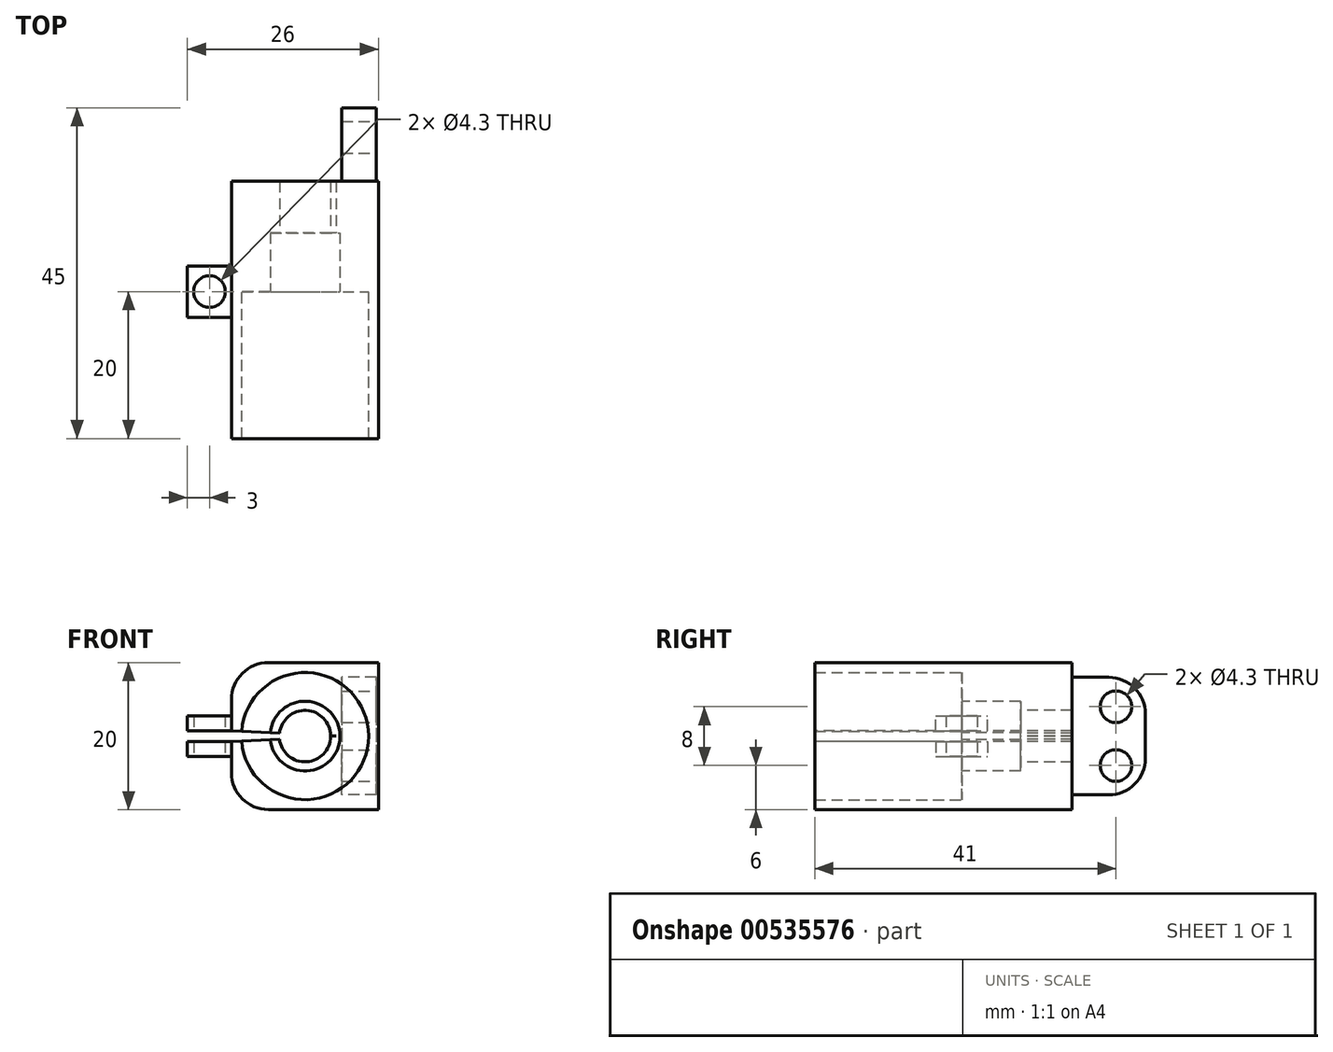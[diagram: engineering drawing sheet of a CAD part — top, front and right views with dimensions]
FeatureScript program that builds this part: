
annotation { "Feature Type Name" : "Feature", "Feature Type Description" : "" }
export const myFeature = defineFeature(function(context is Context, id is Id, definition is map)
    precondition{}
    {
        {
            var Q0;
            Q0=qCreatedBy(makeId("Front.planeOp"),FACE);
            var sketch = newSketch(context, id + "F0", { "sketchPlane" : qUnion([Q0])});
            skCircle(sketch, "E0", {"center": v(0, 0) * mm, "radius": 8.65 * mm});
            skLineSegment(sketch, "E1.bottom", {"start": v(-10, 10) * mm, "end": v(10, 10) * mm});
            skLineSegment(sketch, "E1.top", {"start": v(-10, -10) * mm, "end": v(10, -10) * mm});
            skLineSegment(sketch, "E1.left", {"start": v(-10, 10) * mm, "end": v(-10, -10) * mm});
            skLineSegment(sketch, "E1.right", {"start": v(10, 10) * mm, "end": v(10, -10) * mm});
            skSolve(sketch);
        }
        {
            var Q0;
            Q0=qSketchRegion(id+"F0",true);
            extrude(context, id + "F1", {"entities" : qUnion([Q0]), "depth" : 20 * mm, "offsetDistance" : 25 * mm});
        }
        {
            var Q0;
            Q0=qCreatedBy(makeId("Front.planeOp"),FACE);
            var sketch = newSketch(context, id + "F2", { "sketchPlane" : qUnion([Q0])});
            skLineSegment(sketch, "E2.bottom", {"start": v(10, 10) * mm, "end": v(-10, 10) * mm});
            skLineSegment(sketch, "E2.top", {"start": v(10, -10) * mm, "end": v(-10, -10) * mm});
            skLineSegment(sketch, "E2.left", {"start": v(10, 10) * mm, "end": v(10, -10) * mm});
            skLineSegment(sketch, "E2.right", {"start": v(-10, 10) * mm, "end": v(-10, -10) * mm});
            skPoint(sketch, "E2.middle", {"position": v(0, 0) * mm});
            skSolve(sketch);
        }
        {
            var Q0;
            Q0=qSketchRegion(id+"F2",true);
            extrude(context, id + "F3", {"entities" : qUnion([Q0]), "operationType" : NewBodyOperationType.ADD, "oppositeDirection" : true, "depth" : 15 * mm, "offsetDistance" : 25 * mm});
        }
        {
            var Q0;
            Q0=qCreatedBy(makeId("Front.planeOp"),FACE);
            var sketch = newSketch(context, id + "F4", { "sketchPlane" : qUnion([Q0])});
            skCircle(sketch, "E3", {"center": v(0, 0) * mm, "radius": 4.75 * mm});
            skSolve(sketch);
        }
        {
            var Q0;
            Q0=qSketchRegion(id+"F4",true);
            extrude(context, id + "F5", {"entities" : qUnion([Q0]), "operationType" : NewBodyOperationType.REMOVE, "oppositeDirection" : true, "depth" : 8 * mm, "offsetDistance" : 25 * mm});
        }
        {
            var Q0;
            Q0=qCreatedBy(makeId("Front.planeOp"),FACE);
            var sketch = newSketch(context, id + "F6", { "sketchPlane" : qUnion([Q0])});
            skCircle(sketch, "E4", {"center": v(0, 0) * mm, "radius": 2.08 * mm});
            skSolve(sketch);
        }
        {
            var Q0;
            Q0=qSketchRegion(id+"F6",true);
            extrude(context, id + "F7", {"entities" : qUnion([Q0]), "operationType" : NewBodyOperationType.REMOVE, "oppositeDirection" : true, "depth" : 11 * mm, "offsetDistance" : 25 * mm});
        }
        {
            var Q0;
            Q0=qCreatedBy(makeId("Front.planeOp"),FACE);
            var sketch = newSketch(context, id + "F8", { "sketchPlane" : qUnion([Q0])});
            skLineSegment(sketch, "E5.left", {"start": v(-10, 0.75) * mm, "end": v(-10, -0.75) * mm});
            skLineSegment(sketch, "E6", {"start": v(4.25, 0) * mm, "end": v(-10, 0.75) * mm});
            skLineSegment(sketch, "E7", {"start": v(4.25, 0) * mm, "end": v(-10, -0.75) * mm});
            skSolve(sketch);
        }
        {
            var Q0;
            Q0=qSketchRegion(id+"F8",true);
            extrude(context, id + "F9", {"entities" : qUnion([Q0]), "operationType" : NewBodyOperationType.REMOVE, "oppositeDirection" : true, "depth" : 50.6 * mm, "offsetDistance" : 25 * mm, "symmetric" : true});
        }
        {
            var Q0;
            Q0=qCreatedBy(makeId("Front.planeOp"),FACE);
            var sketch = newSketch(context, id + "F10", { "sketchPlane" : qUnion([Q0])});
            skLineSegment(sketch, "E8.bottom", {"start": v(-10, 0.75) * mm, "end": v(-16, 0.75) * mm});
            skLineSegment(sketch, "E8.top", {"start": v(-10, 2.75) * mm, "end": v(-16, 2.75) * mm});
            skLineSegment(sketch, "E8.left", {"start": v(-10, 0.75) * mm, "end": v(-10, 2.75) * mm});
            skLineSegment(sketch, "E8.right", {"start": v(-16, 0.75) * mm, "end": v(-16, 2.75) * mm});
            skLineSegment(sketch, "E9.bottom", {"start": v(-10, -0.75) * mm, "end": v(-16, -0.75) * mm});
            skLineSegment(sketch, "E9.top", {"start": v(-10, -2.75) * mm, "end": v(-16, -2.75) * mm});
            skLineSegment(sketch, "E9.left", {"start": v(-10, -0.75) * mm, "end": v(-10, -2.75) * mm});
            skLineSegment(sketch, "E9.right", {"start": v(-16, -0.75) * mm, "end": v(-16, -2.75) * mm});
            skSolve(sketch);
        }
        {
            var Q0;
            Q0=qSketchRegion(id+"F10",true);
            extrude(context, id + "F11", {"entities" : qUnion([Q0]), "operationType" : NewBodyOperationType.ADD, "depth" : 7 * mm, "offsetDistance" : 25 * mm, "symmetric" : true});
        }
        {
            var Q0;
            Q0=qCreatedBy(makeId("Top.planeOp"),FACE);
            var sketch = newSketch(context, id + "F12", { "sketchPlane" : qUnion([Q0])});
            skCircle(sketch, "E10", {"center": v(-13, 0) * mm, "radius": 2.15 * mm});
            skSolve(sketch);
        }
        {
            var Q0;
            Q0=qSketchRegion(id+"F12",true);
            extrude(context, id + "F13", {"entities" : qUnion([Q0]), "operationType" : NewBodyOperationType.REMOVE, "depth" : 10.46 * mm, "offsetDistance" : 25 * mm, "symmetric" : true});
        }
        {
            var Q0;
            Q0=qCreatedBy(makeId("Top.planeOp"),FACE);
            var sketch = newSketch(context, id + "F14", { "sketchPlane" : qUnion([Q0])});
            skCircle(sketch, "E11", {"center": v(-13, 0) * mm, "radius": 1.65 * mm});
            skSolve(sketch);
        }
        {
            var Q0;
            Q0=qSketchRegion(id+"F14",true);
            extrude(context, id + "F15", {"entities" : qUnion([Q0]), "operationType" : NewBodyOperationType.REMOVE, "oppositeDirection" : true, "depth" : 6.34 * mm, "offsetDistance" : 25 * mm});
        }
        {
            var Q0;
            Q0=qCreatedBy(makeId("Front.planeOp"),FACE);
            var sketch = newSketch(context, id + "F16", { "sketchPlane" : qUnion([Q0])});
            skCircle(sketch, "E12", {"center": v(0, 0) * mm, "radius": 3.5 * mm});
            skSolve(sketch);
        }
        {
            var Q0;
            Q0=qSketchRegion(id+"F16",true);
            extrude(context, id + "F17", {"entities" : qUnion([Q0]), "operationType" : NewBodyOperationType.REMOVE, "oppositeDirection" : true, "depth" : 31.8 * mm, "offsetDistance" : 25 * mm});
        }
        {
            var Q0;
            Q0=makeQuery(id+"F3.boolean.opBoolean","MERGE",EDGE,{"derivedFrom":[makeQuery(id+"F1.opExtrude","SWEPT_EDGE",EDGE,{"disambiguationData":[OSD([sQuery(id+"F0.wireOp",EDGE,"E1.top"),sQuery(id+"F0.wireOp",EDGE,"E1.left")])]}),makeQuery(id+"F3.opExtrude","SWEPT_EDGE",EDGE,{"disambiguationData":[OSD([sQuery(id+"F2.wireOp",EDGE,"E2.top"),sQuery(id+"F2.wireOp",EDGE,"E2.right")])]})]});
            var Q1;
            Q1=makeQuery(id+"F3.boolean.opBoolean","MERGE",EDGE,{"derivedFrom":[makeQuery(id+"F1.opExtrude","SWEPT_EDGE",EDGE,{"disambiguationData":[OSD([sQuery(id+"F0.wireOp",EDGE,"E1.bottom"),sQuery(id+"F0.wireOp",EDGE,"E1.left")])]}),makeQuery(id+"F3.opExtrude","SWEPT_EDGE",EDGE,{"disambiguationData":[OSD([sQuery(id+"F2.wireOp",EDGE,"E2.bottom"),sQuery(id+"F2.wireOp",EDGE,"E2.right")])]})]});
            fillet(context, id + "F18", {"entities" : qUnion([Q0, Q1]), "radius" : 5 * mm, "tangentPropagation" : true, "allowEdgeOverflow" : false});
        }
        {
            var Q0;
            Q0=qCreatedBy(makeId("Right.planeOp"),FACE);
            var sketch = newSketch(context, id + "F19", { "sketchPlane" : qUnion([Q0])});
            skLineSegment(sketch, "E13.bottom", {"start": v(-55.4, -35) * mm, "end": v(14.6, -35) * mm});
            skLineSegment(sketch, "E13.top", {"start": v(-55.4, 35) * mm, "end": v(14.6, 35) * mm});
            skLineSegment(sketch, "E13.left", {"start": v(-55.4, -35) * mm, "end": v(-55.4, 35) * mm});
            skLineSegment(sketch, "E13.right", {"start": v(14.6, -35) * mm, "end": v(14.6, 35) * mm});
            skPoint(sketch, "E13.middle", {"position": v(-20.4, 0) * mm});
            skSolve(sketch);
        }
        {
            var Q0;
            Q0=qCreatedBy(makeId("Right.planeOp"),FACE);
            var sketch = newSketch(context, id + "F20", { "sketchPlane" : qUnion([Q0])});
            skLineSegment(sketch, "E14.bottom", {"start": v(15, 8) * mm, "end": v(25, 8) * mm});
            skLineSegment(sketch, "E14.top", {"start": v(15, -8) * mm, "end": v(25, -8) * mm});
            skLineSegment(sketch, "E14.left", {"start": v(15, 8) * mm, "end": v(15, -8) * mm});
            skLineSegment(sketch, "E14.right", {"start": v(25, 8) * mm, "end": v(25, -8) * mm});
            skPoint(sketch, "E14.middle", {"position": v(20, 0) * mm});
            skSolve(sketch);
        }
        {
            var Q0;
            Q0 = qSketchRegion(id + "F20", true);
            extrude(context, id + "F21", {"entities" : qUnion([Q0]), "operationType" : NewBodyOperationType.ADD, "depth" : 9.7 * mm, "offsetDistance" : 25 * mm});
        }
        {
            var Q0;
            Q0 = qSketchRegion(id + "F20", true);
            extrude(context, id + "F22", {"entities" : qUnion([Q0]), "operationType" : NewBodyOperationType.REMOVE, "depth" : 5 * mm, "offsetDistance" : 25 * mm});
        }
        {
            var Q0;
            Q0=makeQuery(id+"F19.imprint","IMPRINT",FACE,{"disambiguationData":[TD([[makeQuery(id+"F19.imprint","IMPRINT",EDGE,{"derivedFrom":sQuery(id+"F19.wireOp",EDGE,"E13.bottom")}),1.0]])]});
            var sketch = newSketch(context, id + "F23", { "sketchPlane" : qUnion([Q0])});
            skCircle(sketch, "E15", {"center": v(21, 4) * mm, "radius": 2.15 * mm});
            skCircle(sketch, "E16.MirrorC", {"center": v(21, -4) * mm, "radius": 2.15 * mm});
            skSolve(sketch);
        }
        {
            var Q0;
            Q0 = qSketchRegion(id + "F23", true);
            extrude(context, id + "F24", {"entities" : qUnion([Q0]), "operationType" : NewBodyOperationType.REMOVE, "oppositeDirection" : true, "depth" : 25 * mm, "offsetDistance" : 25 * mm, "symmetric" : true});
        }
        {
            var Q0;
            Q0=makeQuery(id+"F21.opExtrude","SWEPT_EDGE",EDGE,{"disambiguationData":[OSD([sQuery(id+"F20.wireOp",EDGE,"E14.top"),sQuery(id+"F20.wireOp",EDGE,"E14.right")])]});
            var Q1;
            Q1=makeQuery(id+"F21.opExtrude","SWEPT_EDGE",EDGE,{"disambiguationData":[OSD([sQuery(id+"F20.wireOp",EDGE,"E14.bottom"),sQuery(id+"F20.wireOp",EDGE,"E14.right")])]});
            fillet(context, id + "F25", {"entities" : qUnion([Q0, Q1]), "radius" : 5 * mm, "tangentPropagation" : true, "allowEdgeOverflow" : false});
        }
    });
